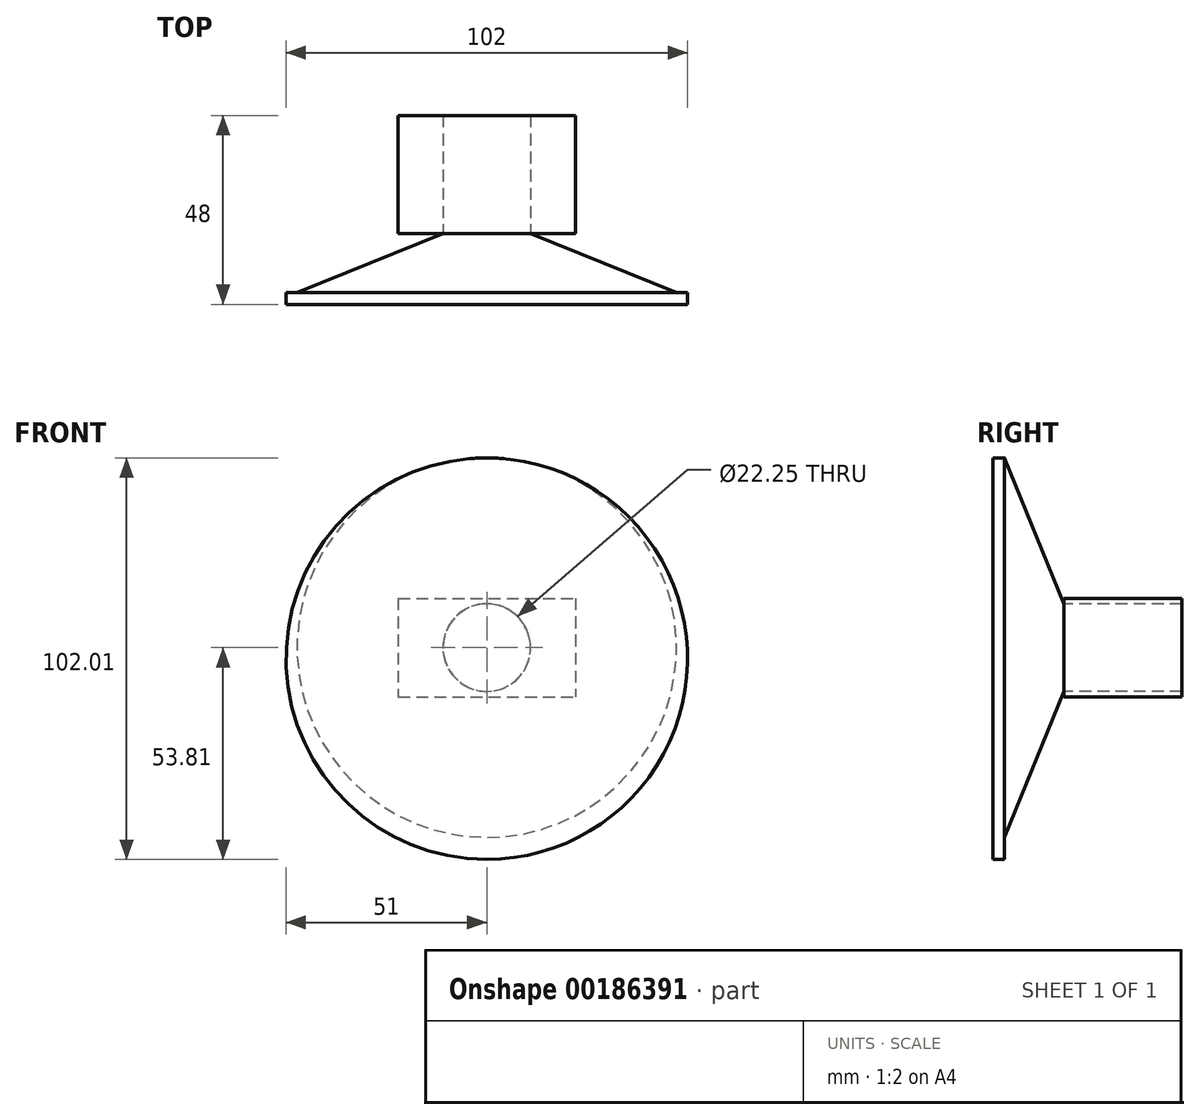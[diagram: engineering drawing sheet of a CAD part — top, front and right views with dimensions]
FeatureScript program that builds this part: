
annotation { "Feature Type Name" : "Feature", "Feature Type Description" : "" }
export const myFeature = defineFeature(function(context is Context, id is Id, definition is map)
    precondition{}
    {
        {
            var Q0;
            Q0=qCreatedBy(makeId("Front.planeOp"),FACE);
            var sketch = newSketch(context, id + "F0", { "sketchPlane" : qUnion([Q0])});
            skCircle(sketch, "E0", {"center": v(0, -2.8) * mm, "radius": 51 * mm});
            skSolve(sketch);
        }
        {
            var Q0;
            Q0=makeQuery(id+"F0.imprint","IMPRINT",FACE,{"disambiguationData":[TD([[makeQuery(id+"F0.imprint","IMPRINT",EDGE,{"derivedFrom":sQuery(id+"F0.wireOp",EDGE,"E0")}),1.0]])]});
            extrude(context, id + "F1", {"entities" : qUnion([Q0]), "depth" : 3 * mm});
        }
        {
            var Q0;
            Q0=qCreatedBy(makeId("Right.planeOp"),FACE);
            var sketch = newSketch(context, id + "F2", { "sketchPlane" : qUnion([Q0])});
            skLineSegment(sketch, "E1", {"start": v(0, 48.2) * mm, "end": v(15, 11.12) * mm});
            skLineSegment(sketch, "E2", {"start": v(0, 0) * mm, "end": v(0, 48.2) * mm});
            skLineSegment(sketch, "E3", {"start": v(15, 11.12) * mm, "end": v(15, 0) * mm});
            skLineSegment(sketch, "E4", {"start": v(15, 0) * mm, "end": v(0, 0) * mm});
            skSolve(sketch);
        }
        {
            var Q0;
            Q0=makeQuery(id+"F2.imprint","IMPRINT",FACE,{"disambiguationData":[TD([[makeQuery(id+"F2.imprint","IMPRINT",EDGE,{"derivedFrom":sQuery(id+"F2.wireOp",EDGE,"E1")}),-1.0]])]});
            var Q1;
            Q1=sQuery(id+"F2.wireOp",EDGE,"E4");
            revolve(context, id + "F3", {"operationType" : NewBodyOperationType.ADD, "entities" : qUnion([Q0]), "axis" : qUnion([Q1]), "revolveType" : RevolveType.FULL});
        }
        {
            var Q0;
            Q0=makeQuery(id+"F3.opRevolve","SWEPT_FACE",FACE,{"disambiguationData":[OSD([sQuery(id+"F2.wireOp",EDGE,"E3")])]});
            var sketch = newSketch(context, id + "F4", { "sketchPlane" : qUnion([Q0])});
            skLineSegment(sketch, "E5.bottom", {"start": v(22.5, 12.5) * mm, "end": v(-22.5, 12.5) * mm});
            skLineSegment(sketch, "E5.top", {"start": v(22.5, -12.5) * mm, "end": v(-22.5, -12.5) * mm});
            skLineSegment(sketch, "E5.left", {"start": v(22.5, 12.5) * mm, "end": v(22.5, -12.5) * mm});
            skLineSegment(sketch, "E5.right", {"start": v(-22.5, 12.5) * mm, "end": v(-22.5, -12.5) * mm});
            skPoint(sketch, "E5.middle", {"position": v(0, 0) * mm});
            skSolve(sketch);
        }
        {
            var Q0;
            Q0=makeQuery(id+"F4.imprint","IMPRINT",FACE,{"disambiguationData":[TD([[makeQuery(id+"F4.imprint","IMPRINT",EDGE,{"derivedFrom":sQuery(id+"F4.wireOp",EDGE,"E5.bottom")}),1.0]])]});
            extrude(context, id + "F5", {"entities" : qUnion([Q0]), "depth" : 30 * mm});
        }
    });
